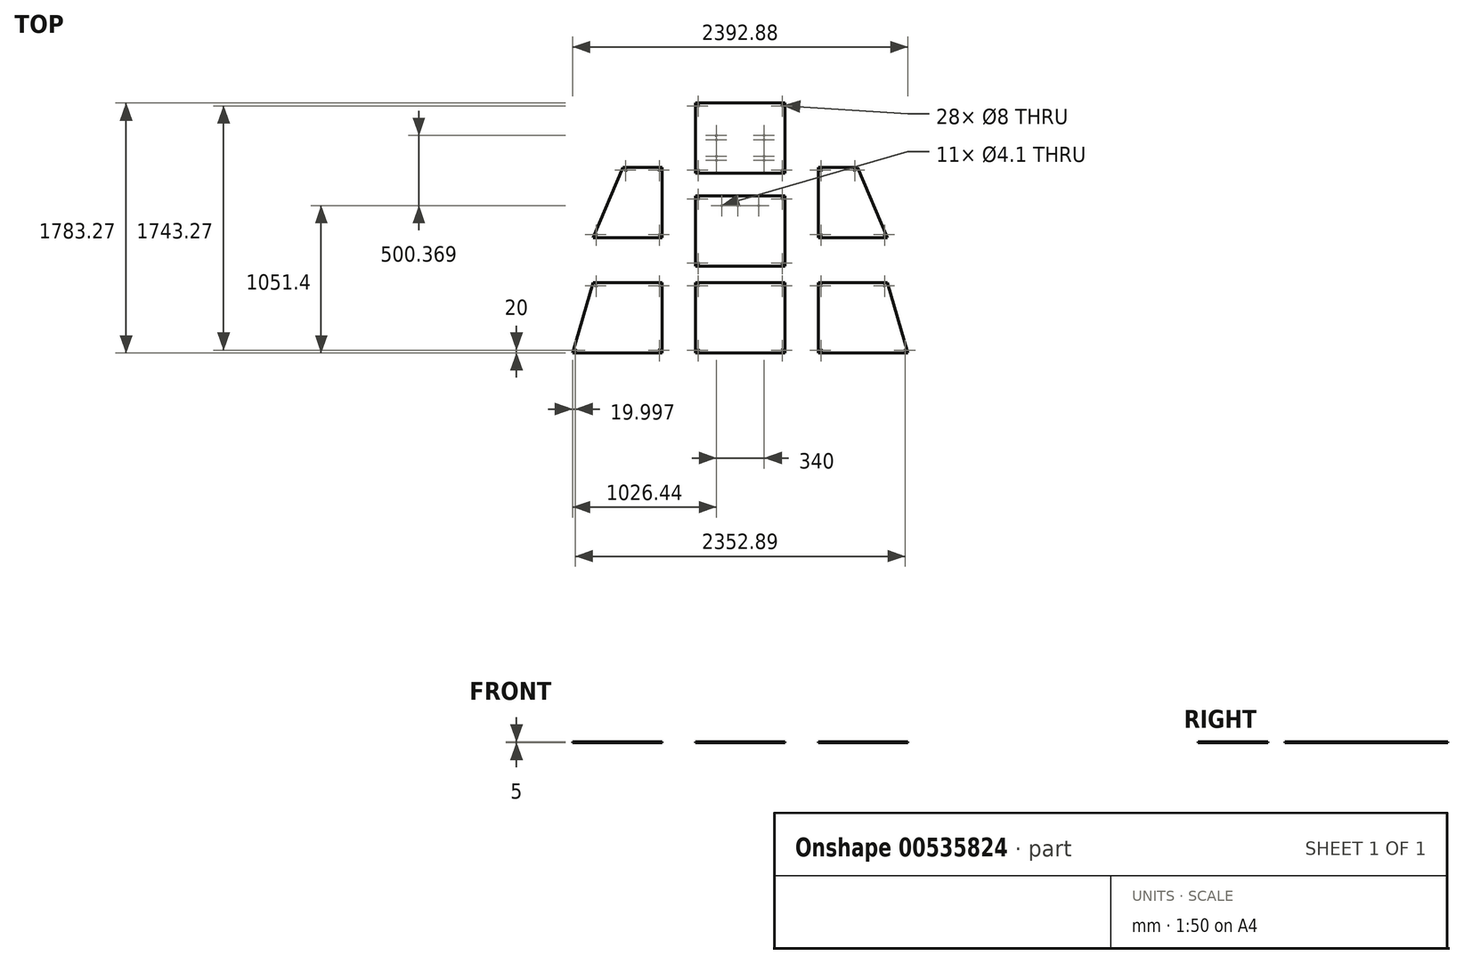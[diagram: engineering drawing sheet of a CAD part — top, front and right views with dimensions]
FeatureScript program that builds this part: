
annotation { "Feature Type Name" : "Feature", "Feature Type Description" : "" }
export const myFeature = defineFeature(function(context is Context, id is Id, definition is map)
    precondition{}
    {
        {
            var Q0;
            Q0=qCreatedBy(makeId("Top.planeOp"),FACE);
            var sketch = newSketch(context, id + "F0", { "sketchPlane" : qUnion([Q0])});
            skLineSegment(sketch, "E0.bottom", {"start": v(320, -250) * mm, "end": v(-320, -250) * mm});
            skLineSegment(sketch, "E0.top", {"start": v(320, 250) * mm, "end": v(-320, 250) * mm});
            skLineSegment(sketch, "E0.left", {"start": v(320, -250) * mm, "end": v(320, 250) * mm});
            skLineSegment(sketch, "E0.right", {"start": v(-320, -250) * mm, "end": v(-320, 250) * mm});
            skPoint(sketch, "E0.middle", {"position": v(0, 0) * mm});
            skCircle(sketch, "E1", {"center": v(300, 230) * mm, "radius": 4 * mm});
            skCircle(sketch, "E2", {"center": v(-300, 230) * mm, "radius": 4 * mm});
            skCircle(sketch, "E3", {"center": v(300, -230) * mm, "radius": 4 * mm});
            skCircle(sketch, "E4", {"center": v(-300, -230) * mm, "radius": 4 * mm});
            skSolve(sketch);
        }
        {
            var Q0;
            Q0=qSketchRegion(id+"F0",true);
            extrude(context, id + "F1", {"entities" : qUnion([Q0]), "depth" : 5 * mm});
        }
        {
            var Q0;
            Q0=qCreatedBy(makeId("Top.planeOp"),FACE);
            var sketch = newSketch(context, id + "F2", { "sketchPlane" : qUnion([Q0])});
            skLineSegment(sketch, "E5.top", {"start": v(-556.44, 250) * mm, "end": v(-1048.94, 250) * mm});
            skLineSegment(sketch, "E5.left", {"start": v(-556.44, -250) * mm, "end": v(-556.44, 250) * mm});
            skPoint(sketch, "E5.middle", {"position": v(-802.7, 0) * mm});
            skLineSegment(sketch, "E6", {"start": v(-556.44, -250) * mm, "end": v(-1196.44, -250) * mm});
            skLineSegment(sketch, "E7", {"start": v(-1196.44, -250) * mm, "end": v(-1048.94, 250) * mm});
            skCircle(sketch, "E8", {"center": v(-576.44, 230) * mm, "radius": 4 * mm});
            skCircle(sketch, "E9", {"center": v(-576.44, -230) * mm, "radius": 4 * mm});
            skCircle(sketch, "E10", {"center": v(-1176.44, -230) * mm, "radius": 4 * mm});
            skCircle(sketch, "E11", {"center": v(-1028.94, 230) * mm, "radius": 4 * mm});
            skLineSegment(sketch, "E12.bottom", {"start": v(-556.44, 573.43) * mm, "end": v(-1048.94, 573.43) * mm});
            skLineSegment(sketch, "E12.left", {"start": v(-556.44, 573.43) * mm, "end": v(-556.44, 1073.43) * mm});
            skPoint(sketch, "E12.middle", {"position": v(-802.7, 823.43) * mm});
            skLineSegment(sketch, "E13", {"start": v(-556.44, 1073.43) * mm, "end": v(-836.44, 1073.43) * mm});
            skLineSegment(sketch, "E14", {"start": v(-1048.94, 573.43) * mm, "end": v(-836.44, 1073.43) * mm});
            skCircle(sketch, "E15", {"center": v(-576.44, 1053.43) * mm, "radius": 4 * mm});
            skCircle(sketch, "E16", {"center": v(-576.44, 593.43) * mm, "radius": 4 * mm});
            skCircle(sketch, "E17", {"center": v(-1028.94, 593.43) * mm, "radius": 4 * mm});
            skCircle(sketch, "E18", {"center": v(-816.44, 1053.43) * mm, "radius": 4 * mm});
            skSolve(sketch);
        }
        {
            var Q0;
            Q0=qSketchRegion(id+"F2",true);
            extrude(context, id + "F3", {"entities" : qUnion([Q0]), "depth" : 5 * mm});
        }
        {
            var Q0;
            Q0=makeQuery(id+"F3.opExtrude","SWEPT_BODY",BODY,{"disambiguationData":[OSD([sQuery(id+"F2.wireOp",EDGE,"E5.top"),sQuery(id+"F2.wireOp",EDGE,"E5.left"),sQuery(id+"F2.wireOp",EDGE,"E6"),sQuery(id+"F2.wireOp",EDGE,"E7"),sQuery(id+"F2.wireOp",EDGE,"E8"),sQuery(id+"F2.wireOp",EDGE,"E9"),sQuery(id+"F2.wireOp",EDGE,"E10"),sQuery(id+"F2.wireOp",EDGE,"E11")])]});
            var Q1;
            Q1=makeQuery(id+"F3.opExtrude","SWEPT_BODY",BODY,{"disambiguationData":[OSD([sQuery(id+"F2.wireOp",EDGE,"E12.bottom"),sQuery(id+"F2.wireOp",EDGE,"E12.left"),sQuery(id+"F2.wireOp",EDGE,"E13"),sQuery(id+"F2.wireOp",EDGE,"E14"),sQuery(id+"F2.wireOp",EDGE,"E15"),sQuery(id+"F2.wireOp",EDGE,"E16"),sQuery(id+"F2.wireOp",EDGE,"E17"),sQuery(id+"F2.wireOp",EDGE,"E18")])]});
            var Q2;
            Q2=qCreatedBy(makeId("Right.planeOp"),FACE);
            mirror(context, id + "F4", {"entities" : qUnion([Q0, Q1]), "mirrorPlane" : qUnion([Q2])});
        }
        {
            var Q0;
            Q0=qCreatedBy(makeId("Top.planeOp"),FACE);
            var sketch = newSketch(context, id + "F5", { "sketchPlane" : qUnion([Q0])});
            skLineSegment(sketch, "E19.bottom", {"start": v(320, 869.9) * mm, "end": v(-320, 869.9) * mm});
            skLineSegment(sketch, "E19.top", {"start": v(320, 369.9) * mm, "end": v(-320, 369.9) * mm});
            skLineSegment(sketch, "E19.left", {"start": v(320, 869.9) * mm, "end": v(320, 369.9) * mm});
            skLineSegment(sketch, "E19.right", {"start": v(-320, 869.9) * mm, "end": v(-320, 369.9) * mm});
            skPoint(sketch, "E19.middle", {"position": v(0, 619.9) * mm});
            skCircle(sketch, "E20", {"center": v(-132.5, 801.4) * mm, "radius": 2.05 * mm});
            skCircle(sketch, "E21", {"center": v(-17.5, 801.4) * mm, "radius": 2.05 * mm});
            skCircle(sketch, "E22", {"center": v(132.5, 801.4) * mm, "radius": 2.05 * mm});
            skCircle(sketch, "E23", {"center": v(-300, 849.9) * mm, "radius": 4 * mm});
            skCircle(sketch, "E24", {"center": v(300, 849.9) * mm, "radius": 4 * mm});
            skCircle(sketch, "E25", {"center": v(-300, 389.9) * mm, "radius": 4 * mm});
            skCircle(sketch, "E26", {"center": v(300, 389.9) * mm, "radius": 4 * mm});
            skSolve(sketch);
        }
        {
            var Q0;
            Q0=qSketchRegion(id+"F5",true);
            extrude(context, id + "F6", {"entities" : qUnion([Q0]), "depth" : 5 * mm});
        }
        {
            var Q0;
            Q0=qCreatedBy(makeId("Top.planeOp"),FACE);
            var sketch = newSketch(context, id + "F7", { "sketchPlane" : qUnion([Q0])});
            skLineSegment(sketch, "E27.bottom", {"start": v(320, 1033.27) * mm, "end": v(-320, 1033.27) * mm});
            skLineSegment(sketch, "E27.top", {"start": v(320, 1533.27) * mm, "end": v(-320, 1533.27) * mm});
            skLineSegment(sketch, "E27.left", {"start": v(320, 1033.27) * mm, "end": v(320, 1533.27) * mm});
            skLineSegment(sketch, "E27.right", {"start": v(-320, 1033.27) * mm, "end": v(-320, 1533.27) * mm});
            skPoint(sketch, "E27.middle", {"position": v(0, 1283.27) * mm});
            skCircle(sketch, "E28", {"center": v(170, 1153.77) * mm, "radius": 2.05 * mm});
            skCircle(sketch, "E29", {"center": v(170, 1123.77) * mm, "radius": 2.05 * mm});
            skCircle(sketch, "E30", {"center": v(170, 1271.77) * mm, "radius": 2.05 * mm});
            skCircle(sketch, "E31", {"center": v(170, 1301.77) * mm, "radius": 2.05 * mm});
            skCircle(sketch, "E32.MirrorC", {"center": v(-170, 1153.77) * mm, "radius": 2.05 * mm});
            skCircle(sketch, "E33.MirrorC", {"center": v(-170, 1271.77) * mm, "radius": 2.05 * mm});
            skCircle(sketch, "E34.MirrorC", {"center": v(-170, 1301.77) * mm, "radius": 2.05 * mm});
            skCircle(sketch, "E35.MirrorC", {"center": v(-170, 1123.77) * mm, "radius": 2.05 * mm});
            skCircle(sketch, "E36", {"center": v(-300, 1513.27) * mm, "radius": 4 * mm});
            skCircle(sketch, "E37", {"center": v(300, 1513.27) * mm, "radius": 4 * mm});
            skCircle(sketch, "E38", {"center": v(-300, 1053.27) * mm, "radius": 4 * mm});
            skCircle(sketch, "E39", {"center": v(300, 1053.27) * mm, "radius": 4 * mm});
            skSolve(sketch);
        }
        {
            var Q0;
            Q0=qSketchRegion(id+"F7",true);
            extrude(context, id + "F8", {"entities" : qUnion([Q0]), "depth" : 5 * mm});
        }
    });
